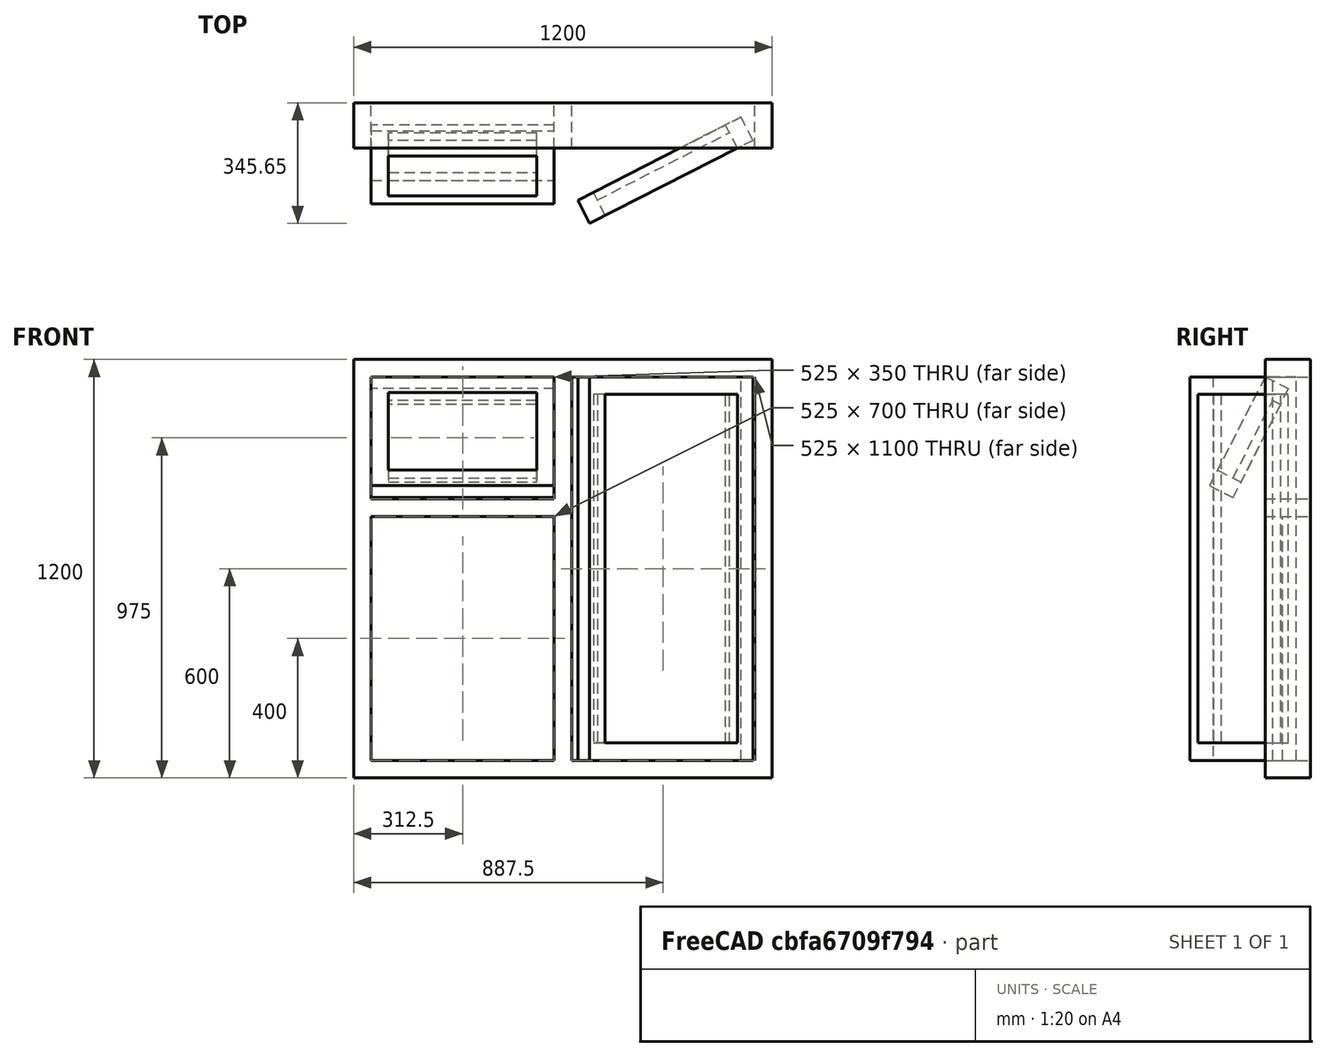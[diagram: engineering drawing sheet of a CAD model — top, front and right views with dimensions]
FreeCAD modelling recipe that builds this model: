
FCSTD DOCUMENT  (FreeCAD 0.19R23578 (Git))
Label: ThreePartRight
License: Creative Commons Attribution-ShareAlike
LicenseURL: http://creativecommons.org/licenses/by-sa/4.0/
objects: Sketcher::SketchObject×1, Part::FeaturePython×1
note: 2 computed .brp shape members not serialized (recipe doc carries the construction recipe); baked Part::Feature solids carry a one-line shape summary decoded from their .brp

FEATURE [Sketcher::SketchObject] Sketch
  Placement = pos=(0,0,0) rot=(1,0,0;1.5708rad)
  expr: .Constraints.FrameOpen = .Constraints.Frame
  expr: .Constraints.WidthSide = (.Constraints.Width - 3 * .Constraints.Frame) / 2
  sketch-geometry (61):
    g0: LineSegment StartX=0 StartY=0 StartZ=0 EndX=1200 EndY=0 EndZ=0
    g1: LineSegment StartX=1200 StartY=0 StartZ=0 EndX=1200 EndY=1200 EndZ=0
    g2: LineSegment StartX=1200 StartY=1200 StartZ=0 EndX=0 EndY=1200 EndZ=0
    g3: LineSegment StartX=0 StartY=1200 StartZ=0 EndX=0 EndY=0 EndZ=0
    g4: LineSegment StartX=50 StartY=50 StartZ=0 EndX=575 EndY=50 EndZ=0
    g5: LineSegment StartX=575 StartY=50 StartZ=0 EndX=575 EndY=750 EndZ=0
    g6: LineSegment StartX=575 StartY=750 StartZ=0 EndX=50 EndY=750 EndZ=0
    g7: LineSegment StartX=50 StartY=750 StartZ=0 EndX=50 EndY=50 EndZ=0
    g8: LineSegment StartX=50 StartY=800 StartZ=0 EndX=575 EndY=800 EndZ=0
    g9: LineSegment StartX=575 StartY=800 StartZ=0 EndX=575 EndY=1150 EndZ=0
    g10: LineSegment StartX=575 StartY=1150 StartZ=0 EndX=50 EndY=1150 EndZ=0
    g11: LineSegment StartX=50 StartY=1150 StartZ=0 EndX=50 EndY=800 EndZ=0
    g12: LineSegment StartX=100 StartY=850 StartZ=0 EndX=525 EndY=850 EndZ=0
    g13: LineSegment StartX=525 StartY=850 StartZ=0 EndX=525 EndY=1100 EndZ=0
    g14: LineSegment StartX=525 StartY=1100 StartZ=0 EndX=100 EndY=1100 EndZ=0
    g15: LineSegment StartX=100 StartY=1100 StartZ=0 EndX=100 EndY=850 EndZ=0
    g16: LineSegment StartX=625 StartY=50 StartZ=0 EndX=1150 EndY=50 EndZ=0
    g17: LineSegment StartX=1150 StartY=50 StartZ=0 EndX=1150 EndY=1150 EndZ=0
    g18: LineSegment StartX=1150 StartY=1150 StartZ=0 EndX=625 EndY=1150 EndZ=0
    g19: LineSegment StartX=625 StartY=1150 StartZ=0 EndX=625 EndY=50 EndZ=0
    g20: LineSegment StartX=675 StartY=100 StartZ=0 EndX=1100 EndY=100 EndZ=0
    g21: LineSegment StartX=1100 StartY=100 StartZ=0 EndX=1100 EndY=1100 EndZ=0
    g22: LineSegment StartX=1100 StartY=1100 StartZ=0 EndX=675 EndY=1100 EndZ=0
    g23: LineSegment StartX=675 StartY=1100 StartZ=0 EndX=675 EndY=100 EndZ=0
    g24: LineSegment StartX=675 StartY=100 StartZ=0 EndX=1100 EndY=100 EndZ=0
    g25: LineSegment StartX=1100 StartY=100 StartZ=0 EndX=1100 EndY=1100 EndZ=0
    g26: LineSegment StartX=1100 StartY=1100 StartZ=0 EndX=675 EndY=1100 EndZ=0
    g27: LineSegment StartX=675 StartY=1100 StartZ=0 EndX=675 EndY=100 EndZ=0
    g28: LineSegment StartX=625 StartY=50 StartZ=0 EndX=1150 EndY=50 EndZ=0
    g29: LineSegment StartX=1150 StartY=50 StartZ=0 EndX=1150 EndY=1150 EndZ=0
    g30: LineSegment StartX=1150 StartY=1150 StartZ=0 EndX=625 EndY=1150 EndZ=0
    g31: LineSegment StartX=625 StartY=1150 StartZ=0 EndX=625 EndY=50 EndZ=0
    g32: LineSegment StartX=50 StartY=50 StartZ=0 EndX=575 EndY=50 EndZ=0
    g33: LineSegment StartX=575 StartY=50 StartZ=0 EndX=575 EndY=750 EndZ=0
    g34: LineSegment StartX=575 StartY=750 StartZ=0 EndX=50 EndY=750 EndZ=0
    g35: LineSegment StartX=50 StartY=750 StartZ=0 EndX=50 EndY=50 EndZ=0
    g36: LineSegment StartX=50 StartY=800 StartZ=0 EndX=575 EndY=800 EndZ=0
    g37: LineSegment StartX=575 StartY=800 StartZ=0 EndX=575 EndY=1150 EndZ=0
    g38: LineSegment StartX=575 StartY=1150 StartZ=0 EndX=50 EndY=1150 EndZ=0
    g39: LineSegment StartX=50 StartY=1150 StartZ=0 EndX=50 EndY=800 EndZ=0
    g40: LineSegment StartX=100 StartY=850 StartZ=0 EndX=525 EndY=850 EndZ=0
    g41: LineSegment StartX=525 StartY=850 StartZ=0 EndX=525 EndY=1100 EndZ=0
    g42: LineSegment StartX=525 StartY=1100 StartZ=0 EndX=100 EndY=1100 EndZ=0
    g43: LineSegment StartX=100 StartY=1100 StartZ=0 EndX=100 EndY=850 EndZ=0
    g44: LineSegment StartX=575 StartY=50 StartZ=0 EndX=625 EndY=50 EndZ=0
    g45: LineSegment StartX=50 StartY=1150 StartZ=0 EndX=50 EndY=1200 EndZ=0
    g46: LineSegment StartX=100 StartY=850 StartZ=0 EndX=100 EndY=800 EndZ=0
    g47: LineSegment StartX=100 StartY=850 StartZ=0 EndX=50 EndY=850 EndZ=0
    g48: LineSegment StartX=50 StartY=750 StartZ=0 EndX=0 EndY=750 EndZ=0
    g49: LineSegment StartX=50 StartY=50 StartZ=0 EndX=50 EndY=0 EndZ=0
    g50: LineSegment StartX=1150 StartY=50 StartZ=0 EndX=1200 EndY=50 EndZ=0
    g51: LineSegment StartX=675 StartY=100 StartZ=0 EndX=625 EndY=100 EndZ=0
    g52: LineSegment StartX=675 StartY=100 StartZ=0 EndX=675 EndY=50 EndZ=0
    g53: LineSegment StartX=1100 StartY=1100 StartZ=0 EndX=1100 EndY=1150 EndZ=0
    g54: LineSegment StartX=1100 StartY=1100 StartZ=0 EndX=1150 EndY=1100 EndZ=0
    g55: LineSegment StartX=525 StartY=1100 StartZ=0 EndX=525 EndY=1150 EndZ=0
    g56: LineSegment StartX=525 StartY=1100 StartZ=0 EndX=575 EndY=1100 EndZ=0
    g57: LineSegment StartX=675 StartY=100 StartZ=0 EndX=675 EndY=50 EndZ=0
    g58: LineSegment StartX=50 StartY=800 StartZ=0 EndX=0 EndY=750 EndZ=0
    g59: LineSegment StartX=50 StartY=1150 StartZ=0 EndX=0 EndY=1200 EndZ=0
    g60: LineSegment StartX=1150 StartY=50 StartZ=0 EndX=1200 EndY=0 EndZ=0
  constraints (167):
    c: Coincident(g0,g1)
    c: Coincident(g1,g2)
    c: Coincident(g2,g3)
    c: Coincident(g3,g0)
    c: Horizontal(g0)
    c: Horizontal(g2)
    c: Vertical(g1)
    c: Vertical(g3)
    c: Coincident(g0,g-1)
    c: Coincident(g4,g5)
    c: Coincident(g5,g6)
    c: Coincident(g6,g7)
    c: Coincident(g7,g4)
    c: Horizontal(g4)
    c: Horizontal(g6)
    c: Vertical(g5)
    c: Vertical(g7)
    c: Coincident(g8,g9)
    c: Coincident(g9,g10)
    c: Coincident(g10,g11)
    c: Coincident(g11,g8)
    c: Horizontal(g8)
    c: Horizontal(g10)
    c: Vertical(g9)
    c: Vertical(g11)
    c: Coincident(g12,g13)
    c: Coincident(g13,g14)
    c: Coincident(g14,g15)
    c: Coincident(g15,g12)
    c: Horizontal(g12)
    c: Horizontal(g14)
    c: Vertical(g13)
    c: Vertical(g15)
    c: Coincident(g16,g17)
    c: Coincident(g17,g18)
    c: Coincident(g18,g19)
    c: Coincident(g19,g16)
    c: Horizontal(g16)
    c: Horizontal(g18)
    c: Vertical(g17)
    c: Vertical(g19)
    c: Coincident(g20,g21)
    c: Coincident(g21,g22)
    c: Coincident(g22,g23)
    c: Coincident(g23,g20)
    c: Horizontal(g20)
    c: Horizontal(g22)
    c: Vertical(g21)
    c: Vertical(g23)
    c: Horizontal(g4,g16)
    c: Horizontal(g9,g18)
    c: Vertical(g8,g5)
    c: DistanceY(g0,g2) = 1200  'Height'
    c: DistanceX(g0,g0) = 1200  'Width'
    c: DistanceY(g8,g10) = 350  'HeightTop'
    c: DistanceX(g18,g17) = 525  'WidthSide'
    c: Coincident(g24,g25)
    c: Coincident(g25,g26)
    c: Coincident(g26,g27)
    c: Coincident(g27,g24)
    c: Horizontal(g24)
    c: Horizontal(g26)
    c: Vertical(g25)
    c: Vertical(g27)
    c: Coincident(g24,g20)
    c: Coincident(g25,g21)
    c: Coincident(g28,g29)
    c: Coincident(g29,g30)
    c: Coincident(g30,g31)
    c: Coincident(g31,g28)
    c: Horizontal(g28)
    c: Horizontal(g30)
    c: Vertical(g29)
    c: Vertical(g31)
    c: Coincident(g28,g16)
    c: Coincident(g29,g17)
    c: Coincident(g32,g33)
    c: Coincident(g33,g34)
    c: Coincident(g34,g35)
    c: Coincident(g35,g32)
    c: Horizontal(g32)
    c: Horizontal(g34)
    c: Vertical(g33)
    c: Vertical(g35)
    c: Coincident(g32,g4)
    c: Coincident(g33,g5)
    c: Coincident(g36,g37)
    c: Coincident(g37,g38)
    c: Coincident(g38,g39)
    c: Coincident(g39,g36)
    c: Horizontal(g36)
    c: Horizontal(g38)
    c: Vertical(g37)
    c: Vertical(g39)
    c: Coincident(g36,g8)
    c: Coincident(g37,g9)
    c: Coincident(g40,g41)
    c: Coincident(g41,g42)
    c: Coincident(g42,g43)
    c: Coincident(g43,g40)
    c: Horizontal(g40)
    c: Horizontal(g42)
    c: Vertical(g41)
    c: Vertical(g43)
    c: Coincident(g40,g12)
    c: Coincident(g41,g13)
    c: Coincident(g44,g32)
    c: Coincident(g44,g28)
    c: Coincident(g45,g38)
    c: PointOnObject(g45,g2)
    c: Vertical(g45)
    c: Coincident(g46,g40)
    c: PointOnObject(g46,g36)
    c: Vertical(g46)
    c: Coincident(g47,g40)
    c: PointOnObject(g47,g39)
    c: Horizontal(g47)
    c: Coincident(g48,g34)
    c: PointOnObject(g48,g3)
    c: Horizontal(g48)
    c: Coincident(g49,g32)
    c: PointOnObject(g49,g0)
    c: Vertical(g49)
    c: PointOnObject(g50,g1)
    c: Horizontal(g50)
    c: Coincident(g51,g24)
    c: PointOnObject(g51,g31)
    c: Horizontal(g51)
    c: Coincident(g52,g24)
    c: PointOnObject(g52,g28)
    c: Vertical(g52)
    c: Coincident(g53,g25)
    c: PointOnObject(g53,g30)
    c: Vertical(g53)
    c: Coincident(g54,g25)
    c: PointOnObject(g54,g29)
    c: Horizontal(g54)
    c: Coincident(g55,g41)
    c: PointOnObject(g55,g38)
    c: Vertical(g55)
    c: Coincident(g56,g41)
    c: PointOnObject(g56,g37)
    c: Horizontal(g56)
    c: Coincident(g50,g28)
    c: DistanceY(g49,g49) = 50  'Frame'
    c: DistanceX(g51,g51) = 50  'FrameOpen'
    c: Equal(g48,g49)
    c: Equal(g56,g46)
    c: Equal(g46,g47)
    c: Equal(g47,g51)
    c: Equal(g51,g54)
    c: Equal(g54,g53)
    c: Equal(g53,g55)
    c: Coincident(g57,g24)
    c: Coincident(g57,g52)
    c: Equal(g52,g51)
    c: Coincident(g58,g36)
    c: Coincident(g58,g48)
    c: Angle(g48,g58) = 0.785398
    c: Vertical(g34,g36)
    c: Equal(g44,g49)
    c: Coincident(g59,g38)
    c: Coincident(g59,g2)
    c: Angle(g45,g59) = 0.785398
    c: Coincident(g60,g28)
    c: Coincident(g60,g0)
    c: Angle(g60,g50) = 0.785398
FEATURE [Part::FeaturePython] Window  # Arch/BIM 170 (typed FeaturePython)
  Area = 0
  Base = -> Sketch
  Frame = 0
  Height = 1200
  HoleDepth = 0
  HoleWire = 1
  HorizontalArea = 0
  IfcData = attributes={"GlobalId": {"name": "GlobalId", "type": "IfcGloballyUniqueId", "is_enum": false, "enum_values": []}, "Description": {"... (+1228 chars omitted),+1 more (map truncated)
  IfcType = 170
  LouvreSpacing = 0
  LouvreWidth = 0
  MoveBase = true
  MoveWithHost = true
  Normal = (0,1,0)
  Opening = 30
  OverallHeight = 1200
  OverallWidth = 0
  PartitioningType = 0
  PerimeterLength = 0
  PredefinedType = 0
  Preset = 0
  SymbolElevation = false
  SymbolPlan = false
  VerticalArea = 0
  Width = 0
  WindowParts = OuterFrame | Frame | Wire0,Wire2,Wire3,Wire4 | 130.0 | 0.0 | FixedGlass | Glass panel | Wire3 | 50.0 | 0.0 | TopFrame | Frame | Wire4,Wire5,Edge19,Mode1 | 75.0 | 0.0 | TopGlass | Glass panel | Wire5 | 50.0 | 0.0 | RightFrame | Frame | Wire2,Wire1,Edge6,Mode1 | 75.0 | 0.0 | RightGlass | Glass panel | Wire1 | 50.0 | 0.0
  expr: OverallHeight = .Height.Value
  expr: OverallWidth = .Width.Value
